# Revit family: QF_HOONVED_HSP4A
name_source: partatom
category: Attrezzature speciali
units: mm (PartAtom-declared; Revit-internal decimal feet)

## family parameters
Basato su piano di lavoro = No
Condiviso = No
Numero OmniClass = 23.40.40.14
Punto di calcolo locali = No
Quota connettore circolare = Usa diametro
Sempre verticale = Sì
Taglio con vuoti quando caricato = No
Tipo di parte = Normale
Titolo OmniClass = Food Service Equipment

## types (1)
- H56601
    Altezza = 673 mm  [stored 2.20801 ft]
    Altezza allacciamento acqua fredda da pavimento finito = 36 mm  [stored 0.11811 ft]
    Altezza allacciamento elettrico da pavimento finito = 47 mm  [stored 0.154199 ft]
    Altezza dello scarico diretto acqua da pavimento finito = 36 mm  [stored 0.11811 ft]
    Corrente di funzionamento normale = 13 A
    Descrizione = SINGLE-PHASE GLASSWASHER WITH WATER SOFTENER
    Diametro condotta acqua fredda = 1"
    Diametro dello scarico diretto di acqua = 1 1/2"
    Fase = 1
    Frequenza = 50 Hz
    Lunghezza = 460 mm  [stored 1.50919 ft]
    Modello = HSP4A
    Numero dei poli = 1
    Peso netto = 37.00 kg
    Pessione minima acqua fredda = 20000.0 Pa
    Potenza elettrica = 3060 W
    Produttore = HOONVED
    Profondità = 521 mm  [stored 1.70932 ft]
    Protezione contro le sovracorrenti = 16 A
    Temperatura raccomandata per acqua fredda = 15 °C
    Tensione = 230 V
    URL = https://www.hoonved.com
    URL catalogo = https://www.hoonved.com

note: [stored X ft] marks values corroborated as IEEE doubles in the binary element streams (Revit-internal decimal feet)

## geometry (parser evidence)
native form markers: Sweep x5
no freeform markers — native parametric forms only
